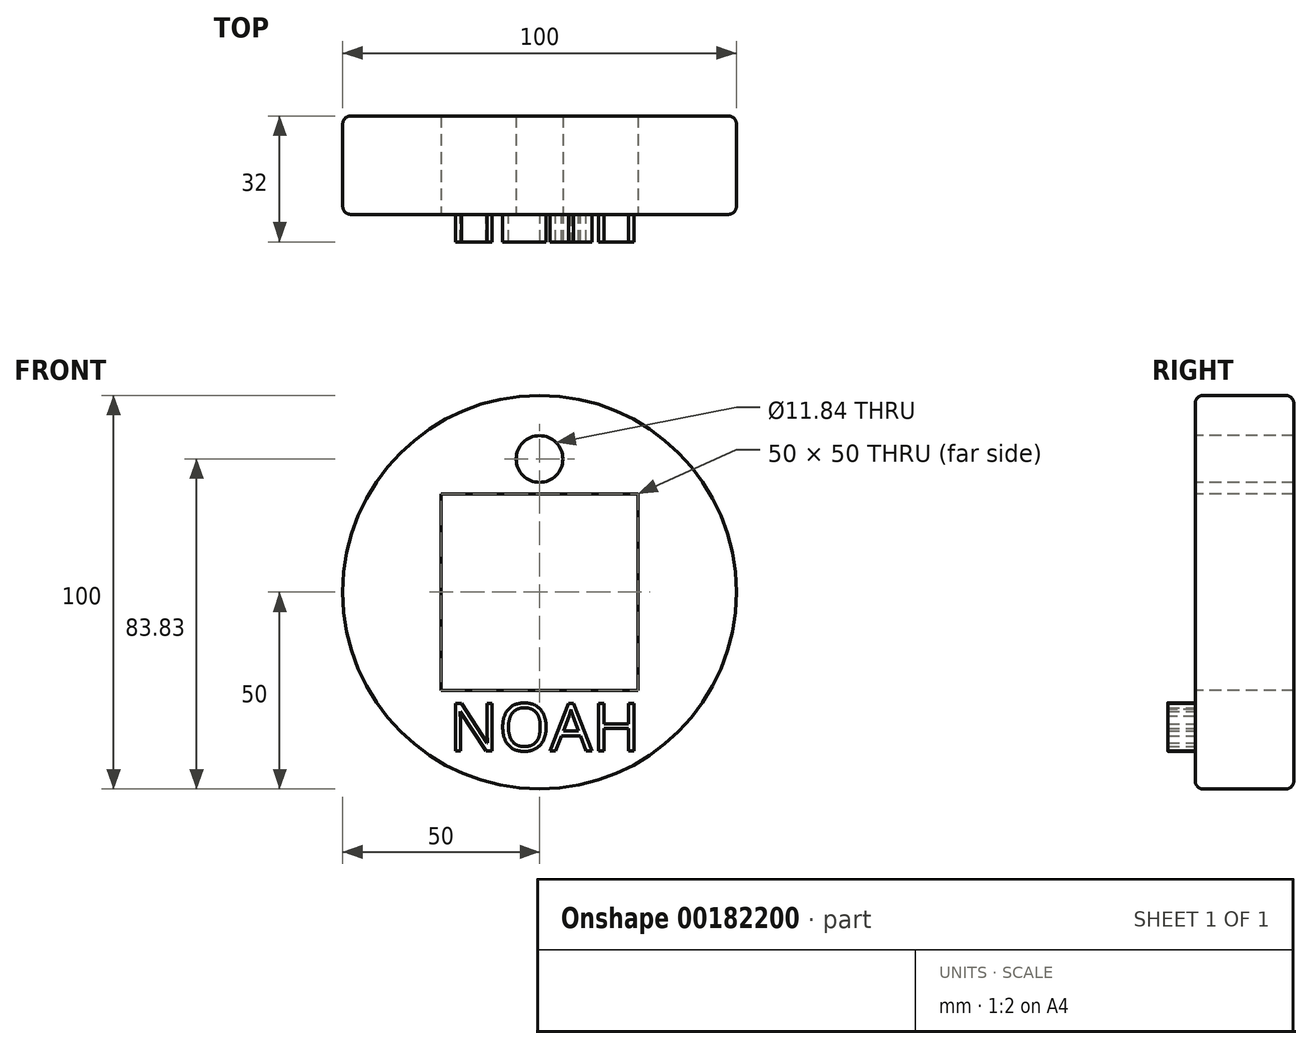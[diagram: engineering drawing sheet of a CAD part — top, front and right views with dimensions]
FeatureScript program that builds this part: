
annotation { "Feature Type Name" : "Feature", "Feature Type Description" : "" }
export const myFeature = defineFeature(function(context is Context, id is Id, definition is map)
    precondition{}
    {
        {
            var Q0;
            Q0=qCreatedBy(makeId("Front.planeOp"),FACE);
            var sketch = newSketch(context, id + "F0", { "sketchPlane" : qUnion([Q0])});
            skCircle(sketch, "E0", {"center": v(0, 0) * mm, "radius": 50 * mm});
            skSolve(sketch);
        }
        {
            var Q0;
            Q0 = qSketchRegion(id + "F0", true);
            extrude(context, id + "F1", {"entities" : qUnion([Q0]), "oppositeDirection" : true, "depth" : 25 * mm});
        }
        {
            var Q0;
            Q0=qCreatedBy(makeId("Front.planeOp"),FACE);
            var sketch = newSketch(context, id + "F2", { "sketchPlane" : qUnion([Q0])});
            skLineSegment(sketch, "E1.bottom", {"start": v(25, -25) * mm, "end": v(-25, -25) * mm});
            skLineSegment(sketch, "E1.top", {"start": v(25, 25) * mm, "end": v(-25, 25) * mm});
            skLineSegment(sketch, "E1.left", {"start": v(25, -25) * mm, "end": v(25, 25) * mm});
            skLineSegment(sketch, "E1.right", {"start": v(-25, -25) * mm, "end": v(-25, 25) * mm});
            skPoint(sketch, "E1.middle", {"position": v(0, 0) * mm});
            skSolve(sketch);
        }
        {
            var Q0;
            Q0 = qSketchRegion(id + "F2", true);
            extrude(context, id + "F3", {"entities" : qUnion([Q0]), "operationType" : NewBodyOperationType.REMOVE, "oppositeDirection" : true, "depth" : 25 * mm});
        }
        {
            var Q0;
            Q0=qCreatedBy(makeId("Front.planeOp"),FACE);
            var sketch = newSketch(context, id + "F4", { "sketchPlane" : qUnion([Q0])});
            skText(sketch, "E2", { "text": "NOAH", "fontName": "OpenSans-Regular.ttf"});
            const initialGuessF4  = {"E2": [-0.02302, -0.04029, 1, 0, 0.01207]};
            skSetInitialGuess(sketch, initialGuessF4);
            skSolve(sketch);
        }
        {
            var Q0;
            Q0 = qSketchRegion(id + "F4", true);
            extrude(context, id + "F5", {"entities" : qUnion([Q0]), "operationType" : NewBodyOperationType.ADD, "depth" : 7 * mm});
        }
        {
            var Q0;
            Q0=makeQuery(id+"F1.opExtrude","CAP_EDGE",EDGE,{"disambiguationData":[OSD([sQuery(id+"F0.wireOp",EDGE,"E0")])],"isStart":true});
            var Q1;
            Q1=makeQuery(id+"F1.opExtrude","CAP_EDGE",EDGE,{"disambiguationData":[OSD([sQuery(id+"F0.wireOp",EDGE,"E0")])],"isStart":false});
            fillet(context, id + "F6", {"entities" : qUnion([Q0, Q1]), "radius" : 2 * mm, "tangentPropagation" : true, "allowEdgeOverflow" : false});
        }
        {
            var Q0;
            {var subQ0=sQuery(id+"F0.wireOp",EDGE,"E0");Q0=makeQuery(id+"F5.boolean.opBoolean","SPLIT",FACE,{"disambiguationData":[TD([makeQuery(id+"F1.opExtrude","SWEPT_FACE",FACE,{"disambiguationData":[OSD([subQ0])]})])],"derivedFrom":makeQuery(id+"F1.opExtrude","CAP_FACE",FACE,{"disambiguationData":[OSD([subQ0])],"isStart":true})});}
            var sketch = newSketch(context, id + "F7", { "sketchPlane" : qUnion([Q0])});
            skCircle(sketch, "E3", {"center": v(0, 33.83) * mm, "radius": 5.92 * mm});
            skSolve(sketch);
        }
        {
            var Q0;
            Q0 = qSketchRegion(id + "F7", true);
            extrude(context, id + "F8", {"entities" : qUnion([Q0]), "operationType" : NewBodyOperationType.REMOVE, "oppositeDirection" : true, "depth" : 26 * mm});
        }
    });
